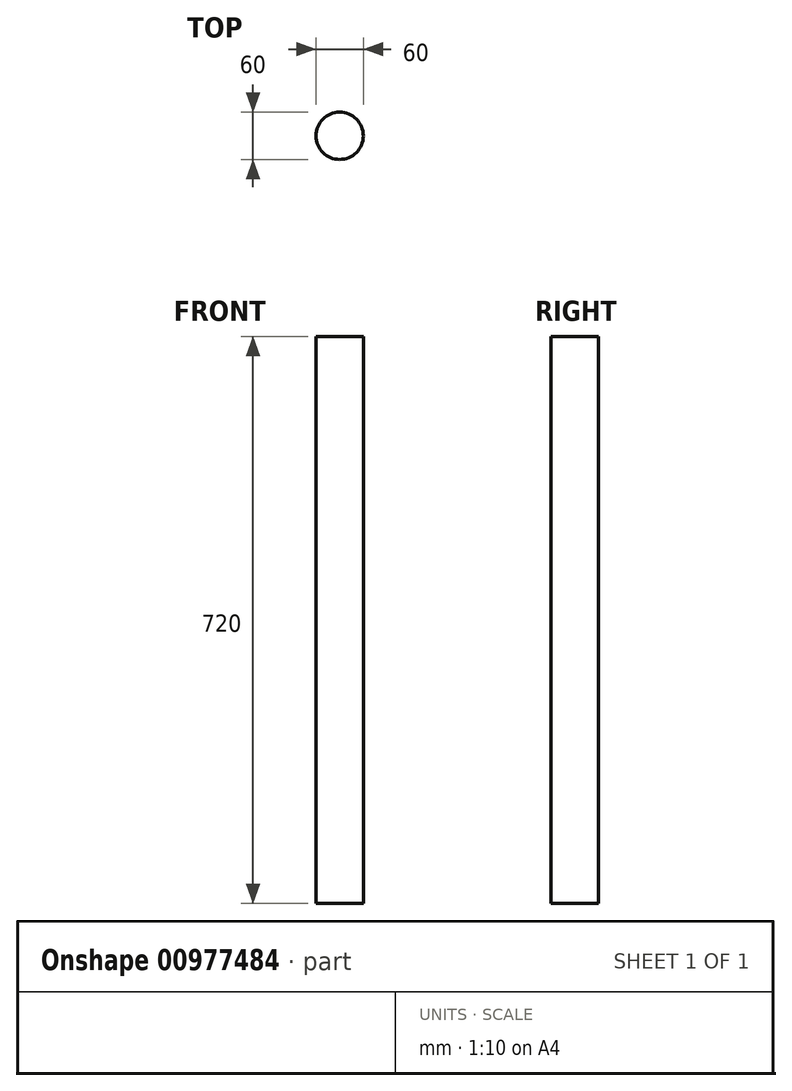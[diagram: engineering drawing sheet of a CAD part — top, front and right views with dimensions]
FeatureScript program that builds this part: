
annotation { "Feature Type Name" : "Feature", "Feature Type Description" : "" }
export const myFeature = defineFeature(function(context is Context, id is Id, definition is map)
    precondition{}
    {
        {
            var Q0;
            Q0=qCreatedBy(makeId("Top.planeOp"),FACE);
            var sketch = newSketch(context, id + "F0", { "sketchPlane" : qUnion([Q0])});
            skCircle(sketch, "E0", {"center": v(0, 0) * mm, "radius": 30 * mm});
            skSolve(sketch);
        }
        {
            var Q0;
            Q0 = qSketchRegion(id + "F0", true);
            extrude(context, id + "F1", {"entities" : qUnion([Q0]), "depth" : 720 * mm, "offsetDistance" : 25 * mm});
        }
    });
